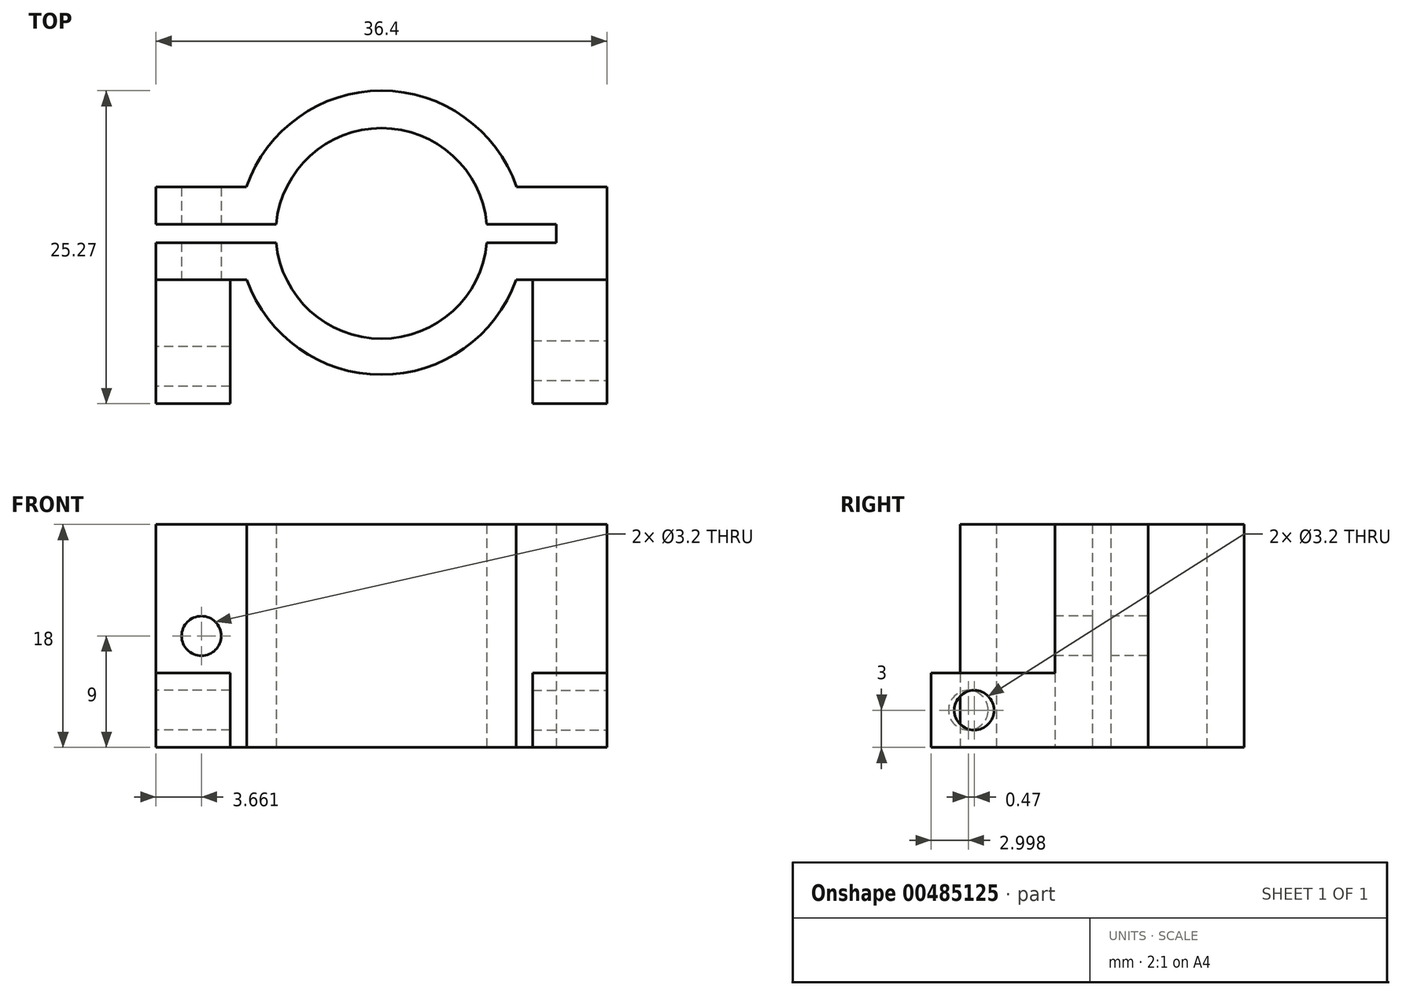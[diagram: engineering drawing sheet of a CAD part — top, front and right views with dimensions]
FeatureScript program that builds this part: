
annotation { "Feature Type Name" : "Feature", "Feature Type Description" : "" }
export const myFeature = defineFeature(function(context is Context, id is Id, definition is map)
    precondition{}
    {
        {
            var Q0;
            Q0=qCreatedBy(makeId("Top.planeOp"),FACE);
            var sketch = newSketch(context, id + "F0", { "sketchPlane" : qUnion([Q0])});
            skLineSegment(sketch, "E0.bottom", {"start": v(-6.7, 13.28) * mm, "end": v(3, 13.28) * mm, "construction": true});
            skLineSegment(sketch, "E0.left", {"start": v(-6.7, 13.28) * mm, "end": v(-6.7, 10.28) * mm, "construction": true});
            skLineSegment(sketch, "E0.right", {"start": v(3, 13.28) * mm, "end": v(3, 10.28) * mm, "construction": true});
            skLineSegment(sketch, "E1.bottom", {"start": v(20, 10.28) * mm, "end": v(29.7, 10.28) * mm, "construction": true});
            skLineSegment(sketch, "E1.top", {"start": v(20, 13.28) * mm, "end": v(33.6, 13.28) * mm, "construction": true});
            skLineSegment(sketch, "E1.left", {"start": v(20, 10.28) * mm, "end": v(20, 13.28) * mm, "construction": true});
            skLineSegment(sketch, "E2", {"start": v(0, 13.28) * mm, "end": v(0, 10.28) * mm, "construction": true});
            skLineSegment(sketch, "E3", {"start": v(23, 13.28) * mm, "end": v(23, 10.28) * mm, "construction": true});
            skLineSegment(sketch, "E4", {"start": v(-6.7, 13.28) * mm, "end": v(3, 13.28) * mm});
            skLineSegment(sketch, "E5", {"start": v(20, 13.28) * mm, "end": v(23, 13.28) * mm});
            skLineSegment(sketch, "E6", {"start": v(20, 13.28) * mm, "end": v(20, 10.28) * mm});
            skLineSegment(sketch, "E7", {"start": v(3, 13.28) * mm, "end": v(3, 10.28) * mm});
            skLineSegment(sketch, "E8", {"start": v(-6.7, 13.28) * mm, "end": v(-6.7, 10.28) * mm});
            skLineSegment(sketch, "E9", {"start": v(29.7, 10.28) * mm, "end": v(23, 10.28) * mm});
            skLineSegment(sketch, "E10.bottom", {"start": v(33.6, 14.78) * mm, "end": v(20, 14.78) * mm, "construction": true});
            skLineSegment(sketch, "E10.top", {"start": v(29.7, 17.78) * mm, "end": v(20, 17.78) * mm, "construction": true});
            skLineSegment(sketch, "E10.right", {"start": v(20, 14.78) * mm, "end": v(20, 17.78) * mm, "construction": true});
            skLineSegment(sketch, "E11", {"start": v(23, 13.28) * mm, "end": v(23, 17.78) * mm, "construction": true});
            skLineSegment(sketch, "E12.bottom", {"start": v(3, 14.78) * mm, "end": v(-6.7, 14.78) * mm, "construction": true});
            skLineSegment(sketch, "E12.top", {"start": v(3, 17.78) * mm, "end": v(-6.7, 17.78) * mm, "construction": true});
            skLineSegment(sketch, "E12.left", {"start": v(3, 14.78) * mm, "end": v(3, 17.78) * mm, "construction": true});
            skLineSegment(sketch, "E12.right", {"start": v(-6.7, 14.78) * mm, "end": v(-6.7, 17.78) * mm, "construction": true});
            skLineSegment(sketch, "E13", {"start": v(20, 14.78) * mm, "end": v(20, 13.28) * mm, "construction": true});
            skPoint(sketch, "E14", {"position": v(20, 14.03) * mm});
            skLineSegment(sketch, "E15", {"start": v(3, 14.78) * mm, "end": v(3, 13.28) * mm, "construction": true});
            skLineSegment(sketch, "E16", {"start": v(3, 14.03) * mm, "end": v(20, 14.03) * mm, "construction": true});
            skPoint(sketch, "E17", {"position": v(11.5, 14.03) * mm});
            skArc(sketch, "E18", {"start": v(20, 14.78) * mm, "mid": v(11.5, 22.54) * mm, "end": v(3, 14.78) * mm, "construction": true});
            skArc(sketch, "E19", {"start": v(3, 13.28) * mm, "mid": v(11.5, 5.48) * mm, "end": v(20, 13.28) * mm, "construction": true});
            skArc(sketch, "E20", {"start": v(0, 13.28) * mm, "mid": v(11.5, 2.57) * mm, "end": v(23, 13.28) * mm, "construction": true});
            skArc(sketch, "E21", {"start": v(23, 14.78) * mm, "mid": v(11.5, 25.58) * mm, "end": v(0, 14.78) * mm, "construction": true});
            skLineSegment(sketch, "E22", {"start": v(25.6, 14.78) * mm, "end": v(25.6, 13.28) * mm, "construction": true});
            skLineSegment(sketch, "E23", {"start": v(-6.7, 10.28) * mm, "end": v(3, 10.28) * mm, "construction": true});
            skLineSegment(sketch, "E24", {"start": v(-6.7, 10.28) * mm, "end": v(0.62, 10.28) * mm});
            skLineSegment(sketch, "E25", {"start": v(-6.7, 14.78) * mm, "end": v(3, 14.78) * mm});
            skLineSegment(sketch, "E26", {"start": v(-6.7, 14.78) * mm, "end": v(-6.7, 17.78) * mm});
            skLineSegment(sketch, "E27", {"start": v(-6.7, 17.78) * mm, "end": v(0.6, 17.78) * mm});
            skLineSegment(sketch, "E28", {"start": v(20, 13.28) * mm, "end": v(25.6, 13.28) * mm});
            skLineSegment(sketch, "E29", {"start": v(25.6, 13.28) * mm, "end": v(25.6, 14.78) * mm});
            skLineSegment(sketch, "E30", {"start": v(25.6, 14.78) * mm, "end": v(20, 14.78) * mm});
            skLineSegment(sketch, "E31", {"start": v(29.7, 17.78) * mm, "end": v(22.4, 17.78) * mm});
            skArc(sketch, "E32", {"start": v(20, 14.78) * mm, "mid": v(11.5, 22.53) * mm, "end": v(3, 14.78) * mm});
            skArc(sketch, "E33", {"start": v(3, 13.28) * mm, "mid": v(11.5, 5.52) * mm, "end": v(20, 13.28) * mm});
            skArc(sketch, "E34", {"start": v(0.62, 10.28) * mm, "mid": v(11.5, 2.62) * mm, "end": v(22.38, 10.28) * mm});
            skArc(sketch, "E35", {"start": v(22.4, 17.78) * mm, "mid": v(11.5, 25.55) * mm, "end": v(0.6, 17.78) * mm});
            skLineSegment(sketch, "E36", {"start": v(29.7, 17.78) * mm, "end": v(29.7, 10.28) * mm});
            skLineSegment(sketch, "E37", {"start": v(23, 10.28) * mm, "end": v(22.38, 10.28) * mm});
            skSolve(sketch);
        }
        {
            var Q0;
            Q0=qSketchRegion(id+"F0",true);
            extrude(context, id + "F1", {"entities" : qUnion([Q0]), "depth" : 18 * mm, "offsetDistance" : 25 * mm});
        }
        {
            var Q0;
            Q0=makeQuery(id+"F1.opExtrude","SWEPT_FACE",FACE,{"disambiguationData":[OSD([sQuery(id+"F0.wireOp",EDGE,"E24")])]});
            var sketch = newSketch(context, id + "F2", { "sketchPlane" : qUnion([Q0])});
            skLineSegment(sketch, "E38.bottom", {"start": v(-6.7, 18) * mm, "end": v(0.62, 18) * mm, "construction": true});
            skLineSegment(sketch, "E38.top", {"start": v(-6.7, 0) * mm, "end": v(0.62, 0) * mm, "construction": true});
            skLineSegment(sketch, "E38.left", {"start": v(-6.7, 18) * mm, "end": v(-6.7, 0) * mm, "construction": true});
            skLineSegment(sketch, "E38.right", {"start": v(0.62, 18) * mm, "end": v(0.62, 0) * mm, "construction": true});
            skLineSegment(sketch, "E39", {"start": v(-3.04, 18) * mm, "end": v(-3.04, 0) * mm, "construction": true});
            skLineSegment(sketch, "E40", {"start": v(-6.7, 9) * mm, "end": v(0.62, 9) * mm, "construction": true});
            skCircle(sketch, "E41", {"center": v(-3.04, 9) * mm, "radius": 0.84 * mm, "construction": true});
            skSolve(sketch);
        }
        {
            var Q0;
            Q0=sQuery(id+"F2.wireOp",VERTEX,"E41.center");
            var Q1;
            Q1=makeQuery(id+"F1.opExtrude","SWEPT_BODY",BODY,{"disambiguationData":[OSD([sQuery(id+"F0.wireOp",EDGE,"E4"),sQuery(id+"F0.wireOp",EDGE,"E8"),sQuery(id+"F0.wireOp",EDGE,"E9"),sQuery(id+"F0.wireOp",EDGE,"E24"),sQuery(id+"F0.wireOp",EDGE,"E25"),sQuery(id+"F0.wireOp",EDGE,"E26"),sQuery(id+"F0.wireOp",EDGE,"E27"),sQuery(id+"F0.wireOp",EDGE,"E28"),sQuery(id+"F0.wireOp",EDGE,"E29"),sQuery(id+"F0.wireOp",EDGE,"E30"),sQuery(id+"F0.wireOp",EDGE,"E31"),sQuery(id+"F0.wireOp",EDGE,"E32"),sQuery(id+"F0.wireOp",EDGE,"E33"),sQuery(id+"F0.wireOp",EDGE,"E34"),sQuery(id+"F0.wireOp",EDGE,"E35"),sQuery(id+"F0.wireOp",EDGE,"E36"),sQuery(id+"F0.wireOp",EDGE,"E37")])]});
            hole(context, id + "F3", {"style" : HoleStyle.SIMPLE, "endStyle" : HoleEndStyle.BLIND, "holeDiameter" : 3.2 * mm, "holeDepth" : 15 * mm, "isTappedThrough" : true, "tappedDepth" : 12 * mm, "tapClearance" : 3, "locations" : qUnion([Q0]), "scope" : qUnion([Q1])});
        }
        {
            var Q0;
            Q0=makeQuery(id+"F1.opExtrude","SWEPT_FACE",FACE,{"disambiguationData":[OSD([sQuery(id+"F0.wireOp",EDGE,"E9"),sQuery(id+"F0.wireOp",EDGE,"E37")])]});
            var sketch = newSketch(context, id + "F4", { "sketchPlane" : qUnion([Q0])});
            skLineSegment(sketch, "E42.bottom", {"start": v(22.38, 0) * mm, "end": v(29.7, 0) * mm, "construction": true});
            skLineSegment(sketch, "E42.top", {"start": v(22.38, 6) * mm, "end": v(29.7, 6) * mm, "construction": true});
            skLineSegment(sketch, "E42.left", {"start": v(22.38, 0) * mm, "end": v(22.38, 6) * mm, "construction": true});
            skLineSegment(sketch, "E42.right", {"start": v(29.7, 0) * mm, "end": v(29.7, 6) * mm, "construction": true});
            skLineSegment(sketch, "E43", {"start": v(23.7, 6) * mm, "end": v(23.7, 0) * mm, "construction": true});
            skLineSegment(sketch, "E44.bottom", {"start": v(23.7, 6) * mm, "end": v(29.7, 6) * mm});
            skLineSegment(sketch, "E44.top", {"start": v(23.7, 0) * mm, "end": v(29.7, 0) * mm});
            skLineSegment(sketch, "E44.left", {"start": v(23.7, 6) * mm, "end": v(23.7, 0) * mm});
            skLineSegment(sketch, "E44.right", {"start": v(29.7, 6) * mm, "end": v(29.7, 0) * mm});
            skSolve(sketch);
        }
        {
            var Q0;
            Q0=makeQuery(id+"F4.imprint","IMPRINT",FACE,{"disambiguationData":[TD([[makeQuery(id+"F4.imprint","IMPRINT",EDGE,{"derivedFrom":sQuery(id+"F4.wireOp",EDGE,"E44.bottom")}),-1.0]])]});
            extrude(context, id + "F5", {"entities" : qUnion([Q0]), "operationType" : NewBodyOperationType.ADD, "depth" : 10 * mm, "offsetDistance" : 25 * mm});
        }
        {
            var Q0;
            Q0=makeQuery(id+"F1.opExtrude","SWEPT_FACE",FACE,{"disambiguationData":[OSD([sQuery(id+"F0.wireOp",EDGE,"E24")])]});
            var sketch = newSketch(context, id + "F6", { "sketchPlane" : qUnion([Q0])});
            skLineSegment(sketch, "E45.bottom", {"start": v(-6.7, 0) * mm, "end": v(0.62, 0) * mm, "construction": true});
            skLineSegment(sketch, "E45.top", {"start": v(-6.7, 6) * mm, "end": v(0.62, 6) * mm, "construction": true});
            skLineSegment(sketch, "E45.left", {"start": v(-6.7, 0) * mm, "end": v(-6.7, 6) * mm, "construction": true});
            skLineSegment(sketch, "E45.right", {"start": v(0.62, 0) * mm, "end": v(0.62, 6) * mm, "construction": true});
            skLineSegment(sketch, "E46", {"start": v(-0.7, 6) * mm, "end": v(-0.7, 0) * mm, "construction": true});
            skLineSegment(sketch, "E47.bottom", {"start": v(-6.7, 6) * mm, "end": v(-0.7, 6) * mm});
            skLineSegment(sketch, "E47.top", {"start": v(-6.7, 0) * mm, "end": v(-0.7, 0) * mm});
            skLineSegment(sketch, "E47.left", {"start": v(-6.7, 6) * mm, "end": v(-6.7, 0) * mm});
            skLineSegment(sketch, "E47.right", {"start": v(-0.7, 6) * mm, "end": v(-0.7, 0) * mm});
            skSolve(sketch);
        }
        {
            var Q0;
            Q0=makeQuery(id+"F6.imprint","IMPRINT",FACE,{"disambiguationData":[TD([[makeQuery(id+"F6.imprint","IMPRINT",EDGE,{"derivedFrom":sQuery(id+"F6.wireOp",EDGE,"E47.bottom")}),-1.0]])]});
            extrude(context, id + "F7", {"entities" : qUnion([Q0]), "operationType" : NewBodyOperationType.ADD, "depth" : 10 * mm, "offsetDistance" : 25 * mm});
        }
        {
            var Q0;
            Q0=makeQuery(id+"F5.boolean.opBoolean","MERGE",FACE,{"derivedFrom":[makeQuery(id+"F1.opExtrude","SWEPT_FACE",FACE,{"disambiguationData":[OSD([sQuery(id+"F0.wireOp",EDGE,"E36")])]}),makeQuery(id+"F5.opExtrude","SWEPT_FACE",FACE,{"disambiguationData":[OSD([sQuery(id+"F4.wireOp",EDGE,"E44.right")])]})]});
            var sketch = newSketch(context, id + "F8", { "sketchPlane" : qUnion([Q0])});
            skLineSegment(sketch, "E48.bottom", {"start": v(0.28, 6) * mm, "end": v(7.22, 6) * mm, "construction": true});
            skLineSegment(sketch, "E48.top", {"start": v(0.28, 0) * mm, "end": v(7.22, 0) * mm, "construction": true});
            skLineSegment(sketch, "E48.left", {"start": v(0.28, 6) * mm, "end": v(0.28, 0) * mm, "construction": true});
            skLineSegment(sketch, "E48.right", {"start": v(7.22, 6) * mm, "end": v(7.22, 0) * mm, "construction": true});
            skLineSegment(sketch, "E49", {"start": v(3.75, 6) * mm, "end": v(3.75, 0) * mm, "construction": true});
            skCircle(sketch, "E50", {"center": v(3.75, 3) * mm, "radius": 0.47 * mm, "construction": true});
            skSolve(sketch);
        }
        {
            var Q0;
            Q0=sQuery(id+"F8.wireOp",VERTEX,"E50.center");
            var Q1;
            Q1=makeQuery(id+"F1.opExtrude","SWEPT_BODY",BODY,{"disambiguationData":[OSD([sQuery(id+"F0.wireOp",EDGE,"E4"),sQuery(id+"F0.wireOp",EDGE,"E8"),sQuery(id+"F0.wireOp",EDGE,"E9"),sQuery(id+"F0.wireOp",EDGE,"E24"),sQuery(id+"F0.wireOp",EDGE,"E25"),sQuery(id+"F0.wireOp",EDGE,"E26"),sQuery(id+"F0.wireOp",EDGE,"E27"),sQuery(id+"F0.wireOp",EDGE,"E28"),sQuery(id+"F0.wireOp",EDGE,"E29"),sQuery(id+"F0.wireOp",EDGE,"E30"),sQuery(id+"F0.wireOp",EDGE,"E31"),sQuery(id+"F0.wireOp",EDGE,"E32"),sQuery(id+"F0.wireOp",EDGE,"E33"),sQuery(id+"F0.wireOp",EDGE,"E34"),sQuery(id+"F0.wireOp",EDGE,"E35"),sQuery(id+"F0.wireOp",EDGE,"E36"),sQuery(id+"F0.wireOp",EDGE,"E37")])]});
            hole(context, id + "F9", {"style" : HoleStyle.SIMPLE, "endStyle" : HoleEndStyle.BLIND, "holeDiameter" : 3.2 * mm, "holeDepth" : 6 * mm, "isTappedThrough" : true, "tappedDepth" : 12 * mm, "tapClearance" : 3, "locations" : qUnion([Q0]), "scope" : qUnion([Q1])});
        }
        {
            var Q0;
            Q0=makeQuery(id+"F7.boolean.opBoolean","MERGE",FACE,{"derivedFrom":[makeQuery(id+"F1.opExtrude","SWEPT_FACE",FACE,{"disambiguationData":[OSD([sQuery(id+"F0.wireOp",EDGE,"E8")])]}),makeQuery(id+"F7.opExtrude","SWEPT_FACE",FACE,{"disambiguationData":[OSD([sQuery(id+"F6.wireOp",EDGE,"E47.left")])]})]});
            var sketch = newSketch(context, id + "F10", { "sketchPlane" : qUnion([Q0])});
            skLineSegment(sketch, "E51.bottom", {"start": v(-0.28, 6) * mm, "end": v(-6.28, 6) * mm, "construction": true});
            skLineSegment(sketch, "E51.top", {"start": v(-0.28, 0) * mm, "end": v(-6.28, 0) * mm, "construction": true});
            skLineSegment(sketch, "E51.left", {"start": v(-0.28, 6) * mm, "end": v(-0.28, 0) * mm, "construction": true});
            skLineSegment(sketch, "E51.right", {"start": v(-6.28, 6) * mm, "end": v(-6.28, 0) * mm, "construction": true});
            skLineSegment(sketch, "E52", {"start": v(-3.28, 6) * mm, "end": v(-3.28, 0) * mm, "construction": true});
            skCircle(sketch, "E53", {"center": v(-3.28, 3) * mm, "radius": 0.68 * mm, "construction": true});
            skSolve(sketch);
        }
        {
            var Q0;
            Q0=sQuery(id+"F10.wireOp",VERTEX,"E53.center");
            var Q1;
            Q1=makeQuery(id+"F1.opExtrude","SWEPT_BODY",BODY,{"disambiguationData":[OSD([sQuery(id+"F0.wireOp",EDGE,"E4"),sQuery(id+"F0.wireOp",EDGE,"E8"),sQuery(id+"F0.wireOp",EDGE,"E9"),sQuery(id+"F0.wireOp",EDGE,"E24"),sQuery(id+"F0.wireOp",EDGE,"E25"),sQuery(id+"F0.wireOp",EDGE,"E26"),sQuery(id+"F0.wireOp",EDGE,"E27"),sQuery(id+"F0.wireOp",EDGE,"E28"),sQuery(id+"F0.wireOp",EDGE,"E29"),sQuery(id+"F0.wireOp",EDGE,"E30"),sQuery(id+"F0.wireOp",EDGE,"E31"),sQuery(id+"F0.wireOp",EDGE,"E32"),sQuery(id+"F0.wireOp",EDGE,"E33"),sQuery(id+"F0.wireOp",EDGE,"E34"),sQuery(id+"F0.wireOp",EDGE,"E35"),sQuery(id+"F0.wireOp",EDGE,"E36"),sQuery(id+"F0.wireOp",EDGE,"E37")])]});
            hole(context, id + "F11", {"style" : HoleStyle.SIMPLE, "endStyle" : HoleEndStyle.BLIND, "holeDiameter" : 3.2 * mm, "holeDepth" : 6 * mm, "isTappedThrough" : true, "tappedDepth" : 12 * mm, "tapClearance" : 3, "locations" : qUnion([Q0]), "scope" : qUnion([Q1])});
        }
    });
